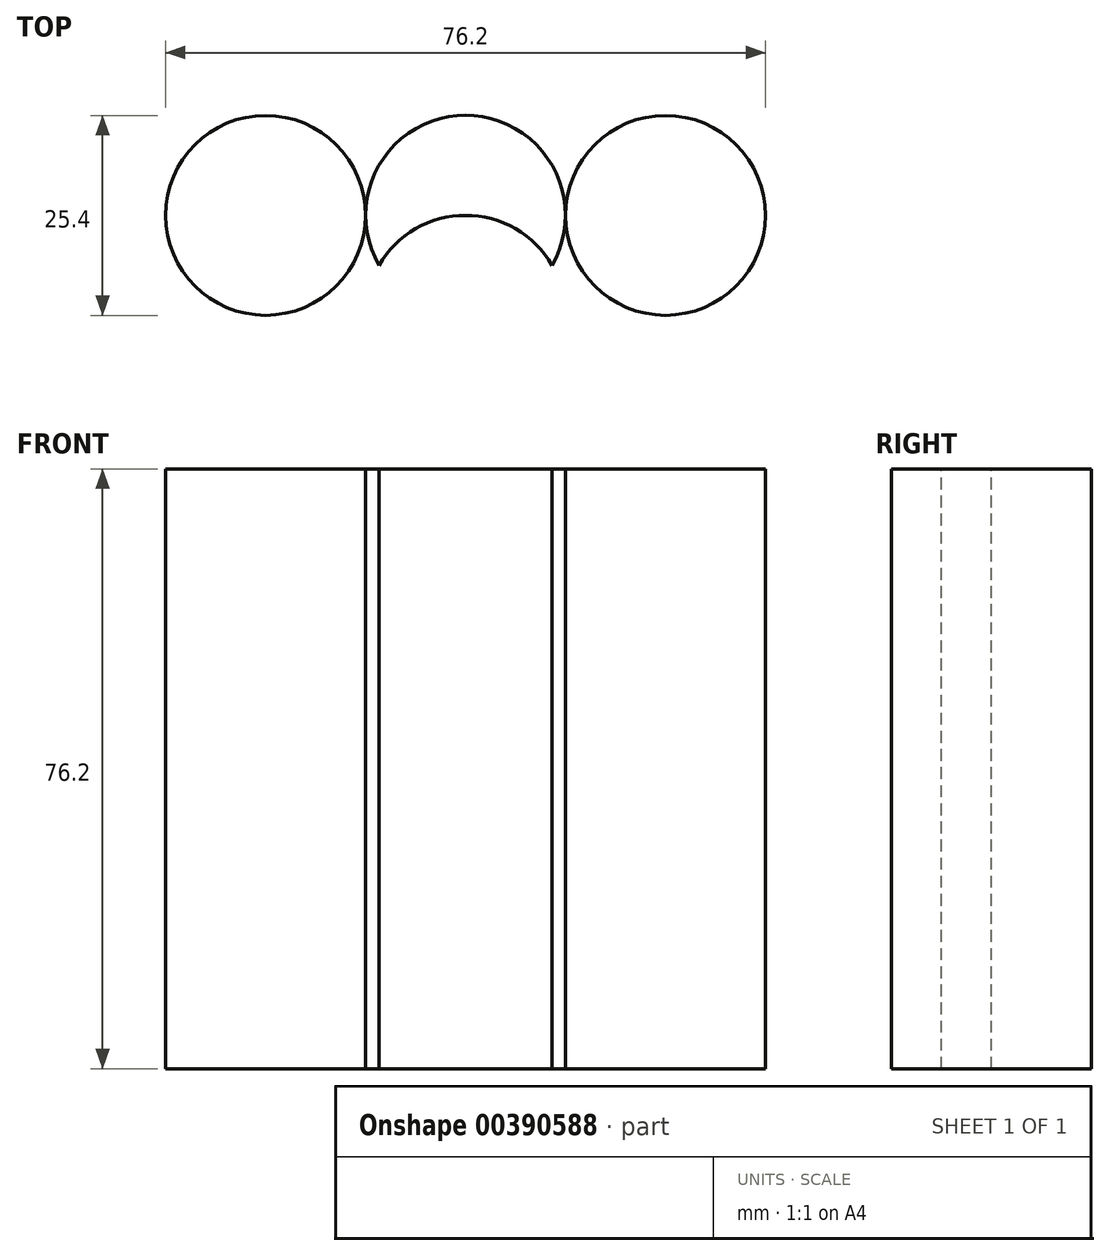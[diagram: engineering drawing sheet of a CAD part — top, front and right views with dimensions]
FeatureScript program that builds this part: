
annotation { "Feature Type Name" : "Feature", "Feature Type Description" : "" }
export const myFeature = defineFeature(function(context is Context, id is Id, definition is map)
    precondition{}
    {
        {
            var Q0;
            Q0=qCreatedBy(makeId("Top.planeOp"),FACE);
            var sketch = newSketch(context, id + "F0", { "sketchPlane" : qUnion([Q0])});
            skCircle(sketch, "E0", {"center": v(0, 0) * mm, "radius": 12.7 * mm});
            skCircle(sketch, "E1.1.0.0", {"center": v(25.4, 0) * mm, "radius": 12.7 * mm});
            skCircle(sketch, "E1.2.0.0", {"center": v(50.8, 0) * mm, "radius": 12.7 * mm});
            skLineSegment(sketch, "E1.direction1", {"start": v(0, 0) * mm, "end": v(25.4, 0) * mm, "construction": true});
            skSolve(sketch);
        }
        {
            var Q0;
            Q0 = qSketchRegion(id + "F0", true);
            extrude(context, id + "F1", {"entities" : qUnion([Q0]), "depth" : 76.2 * mm});
        }
        {
            var Q0;
            Q0=makeQuery(id+"F1.opExtrude","CAP_FACE",FACE,{"disambiguationData":[OSD([sQuery(id+"F0.wireOp",EDGE,"E1.1.0.0")])],"isStart":false});
            var sketch = newSketch(context, id + "F2", { "sketchPlane" : qUnion([Q0])});
            skLineSegment(sketch, "E2", {"start": v(25.4, 0) * mm, "end": v(25.4, -35.26) * mm, "construction": true});
            skCircle(sketch, "E3", {"center": v(25.4, -12.7) * mm, "radius": 12.7 * mm});
            skSolve(sketch);
        }
        {
            var Q0;
            Q0 = qSketchRegion(id + "F2", true);
            extrude(context, id + "F3", {"entities" : qUnion([Q0]), "operationType" : NewBodyOperationType.REMOVE, "oppositeDirection" : true, "depth" : 76.2 * mm});
        }
    });
